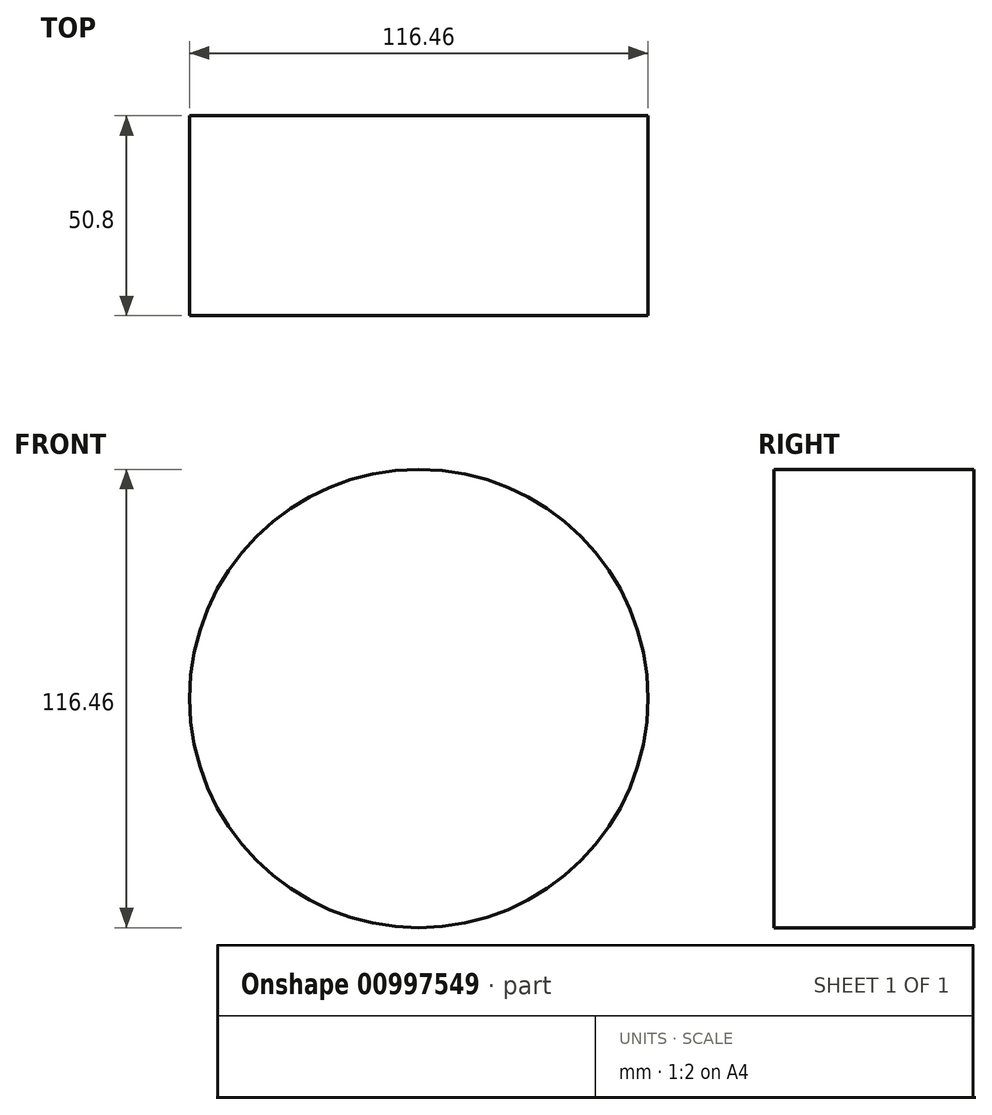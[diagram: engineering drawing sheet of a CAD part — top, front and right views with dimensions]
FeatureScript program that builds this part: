
annotation { "Feature Type Name" : "Feature", "Feature Type Description" : "" }
export const myFeature = defineFeature(function(context is Context, id is Id, definition is map)
    precondition{}
    {
        {
            var Q0;
            Q0=qCreatedBy(makeId("Front.planeOp"),FACE);
            var sketch = newSketch(context, id + "F0", { "sketchPlane" : qUnion([Q0])});
            skCircle(sketch, "E0", {"center": v(0, 0) * mm, "radius": 58.23 * mm});
            skLineSegment(sketch, "E1.bottom", {"start": v(32.81, 48.11) * mm, "end": v(-32.81, 48.11) * mm});
            skLineSegment(sketch, "E1.top", {"start": v(32.81, -48.11) * mm, "end": v(-32.81, -48.11) * mm});
            skLineSegment(sketch, "E1.left", {"start": v(32.81, 48.11) * mm, "end": v(32.81, -48.11) * mm});
            skLineSegment(sketch, "E1.right", {"start": v(-32.81, 48.11) * mm, "end": v(-32.81, -48.11) * mm});
            skSolve(sketch);
        }
        {
            var Q0;
            Q0 = qSketchRegion(id + "F0", true);
            extrude(context, id + "F1", {"entities" : qUnion([Q0]), "depth" : 25.4 * mm, "offsetDistance" : 25.4 * mm});
        }
        {
            var Q0;
            Q0=makeQuery(id+"F1.opExtrude","CAP_FACE",FACE,{"disambiguationData":[OSD([sQuery(id+"F0.wireOp",EDGE,"E0")])],"isStart":false});
            extrude(context, id + "F2", {"entities" : qUnion([Q0]), "operationType" : NewBodyOperationType.ADD, "depth" : 25.4 * mm, "offsetDistance" : 25.4 * mm});
        }
    });
